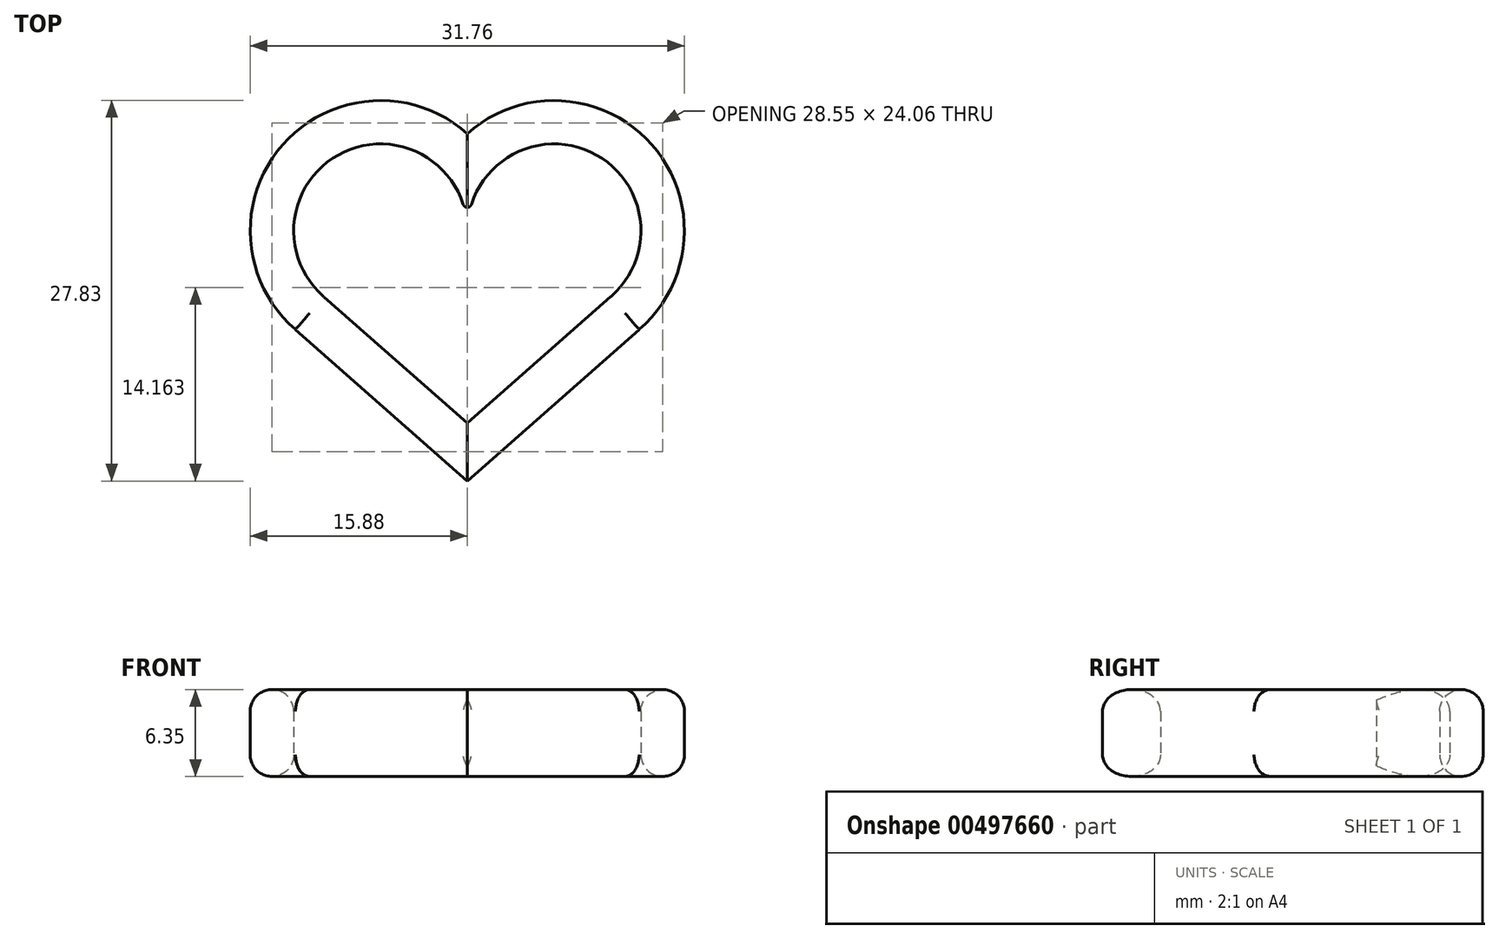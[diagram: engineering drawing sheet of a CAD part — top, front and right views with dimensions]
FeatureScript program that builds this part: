
annotation { "Feature Type Name" : "Feature", "Feature Type Description" : "" }
export const myFeature = defineFeature(function(context is Context, id is Id, definition is map)
    precondition{}
    {
        {
            var Q0;
            Q0=qCreatedBy(makeId("Top.planeOp"),FACE);
            var sketch = newSketch(context, id + "F0", { "sketchPlane" : qUnion([Q0])});
            skArc(sketch, "E0", {"start": v(0, 7.1) * mm, "mid": v(-13.5, 6.29) * mm, "end": v(-12.57, -7.21) * mm});
            skArc(sketch, "E1", {"start": v(0, 7.1) * mm, "mid": v(13.5, 6.29) * mm, "end": v(12.57, -7.21) * mm});
            skLineSegment(sketch, "E2", {"start": v(-12.57, -7.21) * mm, "end": v(0, -18.3) * mm});
            skLineSegment(sketch, "E3", {"start": v(0, -18.3) * mm, "end": v(12.57, -7.21) * mm});
            skArc(sketch, "E4", {"start": v(0, 0) * mm, "mid": v(-9, 5.77) * mm, "end": v(-10.5, -4.8) * mm});
            skArc(sketch, "E5", {"start": v(0, 0) * mm, "mid": v(9, 5.77) * mm, "end": v(10.49, -4.82) * mm});
            skLineSegment(sketch, "E6", {"start": v(10.49, -4.82) * mm, "end": v(0, -14.07) * mm});
            skLineSegment(sketch, "E7", {"start": v(0, -14.07) * mm, "end": v(-10.47, -4.83) * mm});
            skLineSegment(sketch, "E8", {"start": v(-10.47, -4.83) * mm, "end": v(-10.5, -4.8) * mm});
            skSolve(sketch);
        }
        {
            var Q0;
            Q0=makeQuery(id+"F0.imprint","IMPRINT",FACE,{"disambiguationData":[TD([[makeQuery(id+"F0.imprint","IMPRINT",EDGE,{"derivedFrom":sQuery(id+"F0.wireOp",EDGE,"E0")}),1.0]])]});
            extrude(context, id + "F1", {"entities" : qUnion([Q0]), "depth" : 6.35 * mm});
        }
        {
            var Q0;
            Q0=makeQuery(id+"F1.opExtrude","CAP_FACE",FACE,{"disambiguationData":[OSD([sQuery(id+"F0.wireOp",EDGE,"E0"),sQuery(id+"F0.wireOp",EDGE,"E1"),sQuery(id+"F0.wireOp",EDGE,"E2"),sQuery(id+"F0.wireOp",EDGE,"E3")])],"isStart":false});
            var Q1;
            Q1=makeQuery(id+"F1.opExtrude","CAP_FACE",FACE,{"disambiguationData":[OSD([sQuery(id+"F0.wireOp",EDGE,"E0"),sQuery(id+"F0.wireOp",EDGE,"E1"),sQuery(id+"F0.wireOp",EDGE,"E2"),sQuery(id+"F0.wireOp",EDGE,"E3")])],"isStart":true});
            fillet(context, id + "F2", {"entities" : qUnion([Q0, Q1]), "radius" : 1.57 * mm, "tangentPropagation" : true, "allowEdgeOverflow" : false});
        }
        {
            var Q0;
            Q0=makeQuery(id+"F2.opFillet","BLEND_EDGE",EDGE,{"blendedFrom":[makeQuery(id+"F1.opExtrude","CAP_EDGE",EDGE,{"disambiguationData":[OSD([sQuery(id+"F0.wireOp",EDGE,"E0")])],"isStart":false}),makeQuery(id+"F1.opExtrude","CAP_EDGE",EDGE,{"disambiguationData":[OSD([sQuery(id+"F0.wireOp",EDGE,"E2")])],"isStart":false})],"blendedInto":[]});
            var Q1;
            Q1=makeQuery(id+"F2.opFillet","BLEND_EDGE",EDGE,{"blendedFrom":[makeQuery(id+"F1.opExtrude","CAP_EDGE",EDGE,{"disambiguationData":[OSD([sQuery(id+"F0.wireOp",EDGE,"E1")])],"isStart":false}),makeQuery(id+"F1.opExtrude","CAP_EDGE",EDGE,{"disambiguationData":[OSD([sQuery(id+"F0.wireOp",EDGE,"E3")])],"isStart":false})],"blendedInto":[]});
            var Q2;
            Q2=makeQuery(id+"F1.opExtrude","SWEPT_EDGE",EDGE,{"disambiguationData":[OSD([sQuery(id+"F0.wireOp",EDGE,"E0"),sQuery(id+"F0.wireOp",EDGE,"E2")])]});
            var Q3;
            Q3=makeQuery(id+"F1.opExtrude","SWEPT_EDGE",EDGE,{"disambiguationData":[OSD([sQuery(id+"F0.wireOp",EDGE,"E1"),sQuery(id+"F0.wireOp",EDGE,"E3")])]});
            var Q4;
            Q4=makeQuery(id+"F2.opFillet","BLEND_EDGE",EDGE,{"blendedFrom":[makeQuery(id+"F1.opExtrude","CAP_EDGE",EDGE,{"disambiguationData":[OSD([sQuery(id+"F0.wireOp",EDGE,"E0")])],"isStart":true}),makeQuery(id+"F1.opExtrude","CAP_EDGE",EDGE,{"disambiguationData":[OSD([sQuery(id+"F0.wireOp",EDGE,"E2")])],"isStart":true})],"blendedInto":[]});
            var Q5;
            Q5=makeQuery(id+"F2.opFillet","BLEND_EDGE",EDGE,{"blendedFrom":[makeQuery(id+"F1.opExtrude","CAP_EDGE",EDGE,{"disambiguationData":[OSD([sQuery(id+"F0.wireOp",EDGE,"E1")])],"isStart":true}),makeQuery(id+"F1.opExtrude","CAP_EDGE",EDGE,{"disambiguationData":[OSD([sQuery(id+"F0.wireOp",EDGE,"E3")])],"isStart":true})],"blendedInto":[]});
            var Q6;
            Q6=makeQuery(id+"F2.opFillet","BLEND_EDGE",EDGE,{"blendedFrom":[makeQuery(id+"F1.opExtrude","CAP_EDGE",EDGE,{"disambiguationData":[OSD([sQuery(id+"F0.wireOp",EDGE,"E5")])],"isStart":false}),makeQuery(id+"F1.opExtrude","CAP_EDGE",EDGE,{"disambiguationData":[OSD([sQuery(id+"F0.wireOp",EDGE,"E6")])],"isStart":false})],"blendedInto":[]});
            var Q7;
            Q7=makeQuery(id+"F2.opFillet","BLEND_EDGE",EDGE,{"blendedFrom":[makeQuery(id+"F1.opExtrude","CAP_EDGE",EDGE,{"disambiguationData":[OSD([sQuery(id+"F0.wireOp",EDGE,"E4")])],"isStart":false}),makeQuery(id+"F1.opExtrude","CAP_EDGE",EDGE,{"disambiguationData":[OSD([sQuery(id+"F0.wireOp",EDGE,"E8")])],"isStart":false})],"blendedInto":[]});
            var Q8;
            Q8=makeQuery(id+"F1.opExtrude","SWEPT_EDGE",EDGE,{"disambiguationData":[OSD([sQuery(id+"F0.wireOp",EDGE,"E5"),sQuery(id+"F0.wireOp",EDGE,"E6")])]});
            var Q9;
            Q9=makeQuery(id+"F2.opFillet","BLEND_EDGE",EDGE,{"blendedFrom":[makeQuery(id+"F1.opExtrude","CAP_EDGE",EDGE,{"disambiguationData":[OSD([sQuery(id+"F0.wireOp",EDGE,"E5")])],"isStart":true}),makeQuery(id+"F1.opExtrude","CAP_EDGE",EDGE,{"disambiguationData":[OSD([sQuery(id+"F0.wireOp",EDGE,"E6")])],"isStart":true})],"blendedInto":[]});
            var Q10;
            Q10=makeQuery(id+"F2.opFillet","BLEND_EDGE",EDGE,{"blendedFrom":[makeQuery(id+"F1.opExtrude","CAP_EDGE",EDGE,{"disambiguationData":[OSD([sQuery(id+"F0.wireOp",EDGE,"E7")])],"isStart":true}),makeQuery(id+"F1.opExtrude","CAP_EDGE",EDGE,{"disambiguationData":[OSD([sQuery(id+"F0.wireOp",EDGE,"E8")])],"isStart":true})],"blendedInto":[]});
            var Q11;
            Q11=makeQuery(id+"F1.opExtrude","SWEPT_EDGE",EDGE,{"disambiguationData":[OSD([sQuery(id+"F0.wireOp",EDGE,"E7"),sQuery(id+"F0.wireOp",EDGE,"E8")])]});
            fillet(context, id + "F3", {"entities" : qUnion([Q0, Q1, Q2, Q3, Q4, Q5, Q6, Q7, Q8, Q9, Q10, Q11]), "radius" : 2.54 * mm, "tangentPropagation" : true, "allowEdgeOverflow" : false});
        }
        {
            var Q0;
            Q0=makeQuery(id+"F1.opExtrude","SWEPT_EDGE",EDGE,{"disambiguationData":[OSD([sQuery(id+"F0.wireOp",EDGE,"E4"),sQuery(id+"F0.wireOp",EDGE,"E5")])]});
            fillet(context, id + "F4", {"entities" : qUnion([Q0]), "radius" : 0.32 * mm, "tangentPropagation" : true, "allowEdgeOverflow" : false});
        }
    });
